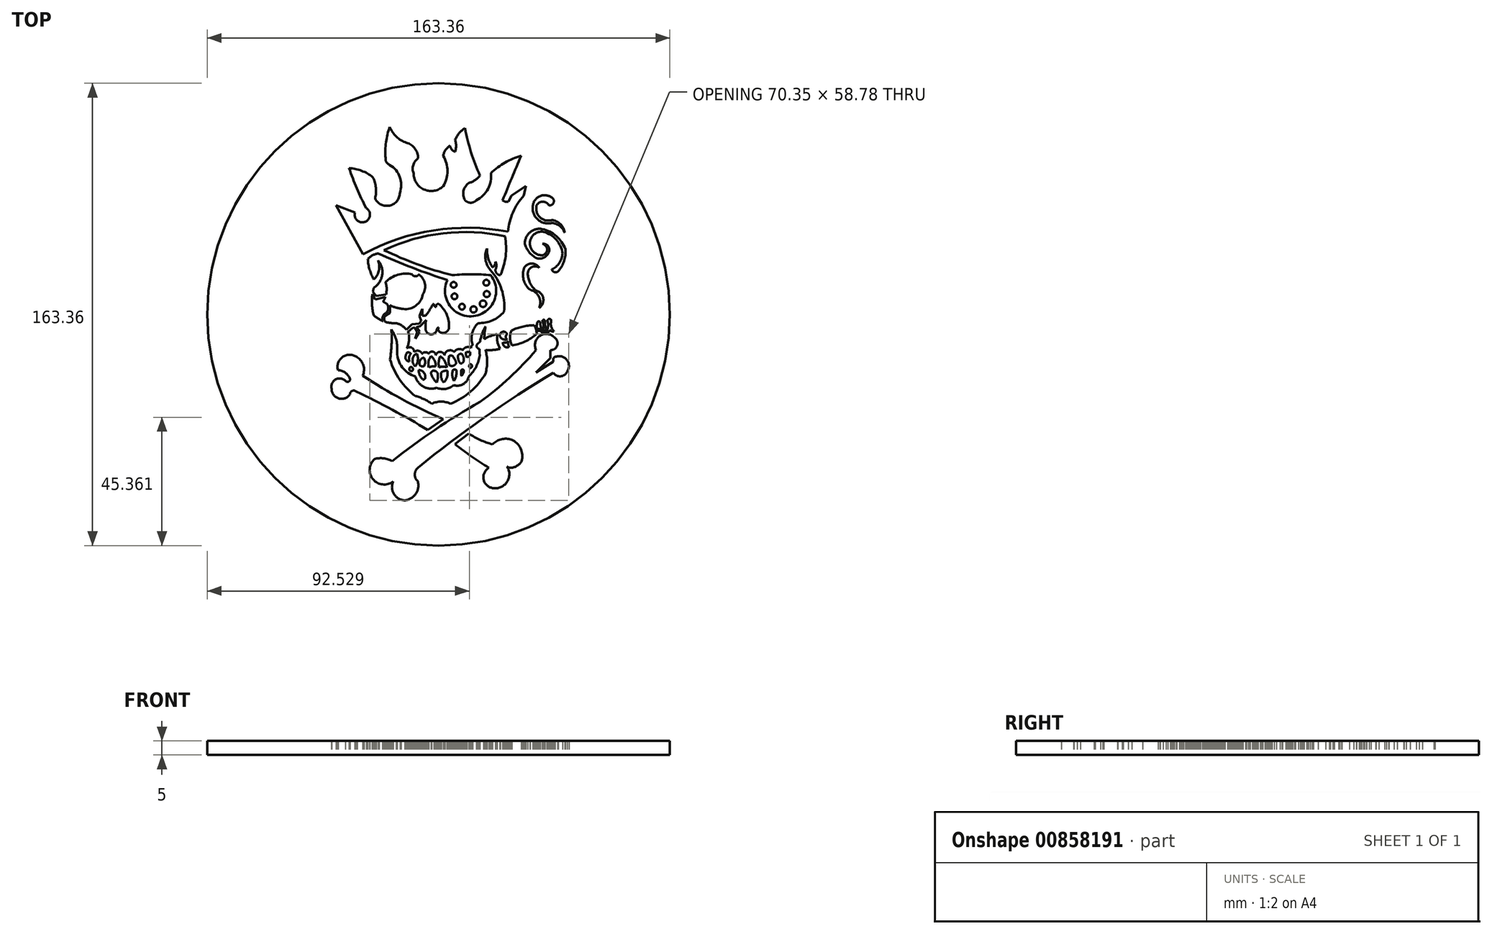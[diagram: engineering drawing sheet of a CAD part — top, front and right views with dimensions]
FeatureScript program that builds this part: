
annotation { "Feature Type Name" : "Feature", "Feature Type Description" : "" }
export const myFeature = defineFeature(function(context is Context, id is Id, definition is map)
    precondition{}
    {
        {
            var Q0;
            Q0=qCreatedBy(makeId("Top.planeOp"),FACE);
            var sketch = newSketch(context, id + "F0", { "sketchPlane" : qUnion([Q0])});
            skArc(sketch, "E0", {"start": v(13.8, 25.5) * mm, "mid": v(-12.46, 25.97) * mm, "end": v(-37.31, 17.5) * mm});
            skLineSegment(sketch, "E1", {"start": v(-37.31, 17.5) * mm, "end": v(-46.9, 34.83) * mm});
            skLineSegment(sketch, "E2", {"start": v(-46.9, 34.83) * mm, "end": v(-40.16, 32.25) * mm});
            skArc(sketch, "E3", {"start": v(-40.16, 32.25) * mm, "mid": v(-36.57, 28.99) * mm, "end": v(-36.23, 33.82) * mm});
            skArc(sketch, "E4", {"start": v(-42.3, 47.97) * mm, "mid": v(-39.5, 40.8) * mm, "end": v(-36.23, 33.82) * mm});
            skArc(sketch, "E5", {"start": v(-33.87, 44.72) * mm, "mid": v(-37.82, 47.02) * mm, "end": v(-42.3, 47.97) * mm});
            skArc(sketch, "E6", {"start": v(-33.08, 37.2) * mm, "mid": v(-32.8, 41.02) * mm, "end": v(-33.87, 44.72) * mm});
            skArc(sketch, "E7", {"start": v(-33.08, 37.2) * mm, "mid": v(-27.9, 34.75) * mm, "end": v(-24.32, 39.21) * mm});
            skArc(sketch, "E8", {"start": v(-24.32, 39.21) * mm, "mid": v(-24.35, 44.8) * mm, "end": v(-27.9, 49.1) * mm});
            skPoint(sketch, "E8.endSnap0", {"position": v(-27.9, 34.75) * mm});
            skArc(sketch, "E9", {"start": v(-29.37, 51.56) * mm, "mid": v(-29.09, 50.06) * mm, "end": v(-27.9, 49.1) * mm});
            skArc(sketch, "E10", {"start": v(-27.9, 62.52) * mm, "mid": v(-29.24, 57.12) * mm, "end": v(-29.37, 51.56) * mm});
            skArc(sketch, "E11", {"start": v(-27.9, 62.52) * mm, "mid": v(-25.56, 59.08) * mm, "end": v(-22, 56.93) * mm});
            skArc(sketch, "E12", {"start": v(-17.88, 51.45) * mm, "mid": v(-19, 54.89) * mm, "end": v(-22, 56.93) * mm});
            skArc(sketch, "E13", {"start": v(-17.88, 51.45) * mm, "mid": v(-19.62, 49.04) * mm, "end": v(-19.46, 46.07) * mm});
            skArc(sketch, "E14", {"start": v(-19.46, 46.07) * mm, "mid": v(-15.74, 40.37) * mm, "end": v(-9.03, 41.54) * mm});
            skArc(sketch, "E15", {"start": v(-9.03, 41.54) * mm, "mid": v(-7.5, 46.92) * mm, "end": v(-9.03, 52.3) * mm});
            skArc(sketch, "E16", {"start": v(-6.6, 55.88) * mm, "mid": v(-8.21, 54.36) * mm, "end": v(-9.03, 52.3) * mm});
            skArc(sketch, "E17", {"start": v(-6.6, 55.88) * mm, "mid": v(-6.01, 54.55) * mm, "end": v(-4.8, 53.72) * mm});
            skArc(sketch, "E18", {"start": v(-4.8, 53.72) * mm, "mid": v(-4.48, 55.86) * mm, "end": v(-4.8, 57.99) * mm});
            skArc(sketch, "E19", {"start": v(-1.33, 62.1) * mm, "mid": v(-3.4, 60.32) * mm, "end": v(-4.8, 57.99) * mm});
            skArc(sketch, "E20", {"start": v(-1.33, 62.1) * mm, "mid": v(0.8, 53.56) * mm, "end": v(3.94, 45.34) * mm});
            skArc(sketch, "E21", {"start": v(0, 42.7) * mm, "mid": v(2.2, 43.68) * mm, "end": v(3.94, 45.34) * mm});
            skArc(sketch, "E22", {"start": v(0, 42.7) * mm, "mid": v(-1.87, 39.9) * mm, "end": v(-1.33, 36.59) * mm});
            skArc(sketch, "E23", {"start": v(-1.33, 36.59) * mm, "mid": v(0.67, 35.74) * mm, "end": v(2.67, 36.59) * mm});
            skArc(sketch, "E24", {"start": v(2.67, 36.59) * mm, "mid": v(6.78, 40.63) * mm, "end": v(7.84, 46.29) * mm});
            skArc(sketch, "E25", {"start": v(18.48, 52.3) * mm, "mid": v(12.8, 49.92) * mm, "end": v(7.84, 46.29) * mm});
            skArc(sketch, "E26", {"start": v(18.48, 52.3) * mm, "mid": v(15.18, 44.46) * mm, "end": v(11.95, 36.59) * mm});
            skArc(sketch, "E27", {"start": v(11.95, 36.59) * mm, "mid": v(12.92, 36.1) * mm, "end": v(14, 36.13) * mm});
            skLineSegment(sketch, "E28", {"start": v(14, 36.13) * mm, "end": v(15.12, 38.22) * mm});
            skLineSegment(sketch, "E29", {"start": v(15.12, 38.22) * mm, "end": v(20.17, 41.67) * mm});
            skLineSegment(sketch, "E30", {"start": v(20.17, 41.67) * mm, "end": v(19.45, 38.22) * mm});
            skArc(sketch, "E31", {"start": v(19.45, 38.22) * mm, "mid": v(15.6, 32.32) * mm, "end": v(13.8, 25.5) * mm});
            skLineSegment(sketch, "E32", {"start": v(-36.21, 27.7) * mm, "end": v(-36.21, 24.14) * mm});
            skLineSegment(sketch, "E33", {"start": v(-36.21, 24.14) * mm, "end": v(-33.76, 22.8) * mm});
            skLineSegment(sketch, "E34", {"start": v(-33.76, 22.8) * mm, "end": v(-33.76, 26.36) * mm});
            skLineSegment(sketch, "E35", {"start": v(-33.76, 26.36) * mm, "end": v(-36.21, 27.7) * mm});
            skLineSegment(sketch, "E36", {"start": v(-26.55, 33.4) * mm, "end": v(-26.55, 29.53) * mm});
            skLineSegment(sketch, "E37", {"start": v(-26.55, 29.53) * mm, "end": v(-24.1, 27.7) * mm});
            skLineSegment(sketch, "E38", {"start": v(-24.1, 27.7) * mm, "end": v(-23.14, 31.27) * mm});
            skLineSegment(sketch, "E39", {"start": v(-23.14, 31.27) * mm, "end": v(-26.55, 33.4) * mm});
            skLineSegment(sketch, "E40", {"start": v(-13.16, 38.56) * mm, "end": v(-15.14, 33.4) * mm});
            skLineSegment(sketch, "E41", {"start": v(-15.14, 33.4) * mm, "end": v(-12.37, 30.32) * mm});
            skLineSegment(sketch, "E42", {"start": v(-12.37, 30.32) * mm, "end": v(-9.75, 34.68) * mm});
            skLineSegment(sketch, "E43", {"start": v(-9.75, 34.68) * mm, "end": v(-13.16, 38.56) * mm});
            skLineSegment(sketch, "E44", {"start": v(0, 34.68) * mm, "end": v(-1.75, 32.46) * mm});
            skLineSegment(sketch, "E45", {"start": v(-1.75, 32.46) * mm, "end": v(-0.13, 29.53) * mm});
            skLineSegment(sketch, "E46", {"start": v(-0.13, 29.53) * mm, "end": v(1.42, 32.3) * mm});
            skLineSegment(sketch, "E47", {"start": v(1.42, 32.3) * mm, "end": v(0, 34.68) * mm});
            skLineSegment(sketch, "E48", {"start": v(11.4, 34.68) * mm, "end": v(9.26, 32.38) * mm});
            skLineSegment(sketch, "E49", {"start": v(9.26, 32.38) * mm, "end": v(9.98, 28.9) * mm});
            skLineSegment(sketch, "E50", {"start": v(9.98, 28.9) * mm, "end": v(12.75, 31.27) * mm});
            skLineSegment(sketch, "E51", {"start": v(12.75, 31.27) * mm, "end": v(11.4, 34.68) * mm});
            skArc(sketch, "E52", {"start": v(12.76, 23.86) * mm, "mid": v(-8.99, 24.94) * mm, "end": v(-29.94, 19) * mm});
            skArc(sketch, "E53", {"start": v(-29.94, 19) * mm, "mid": v(-18.11, 13.95) * mm, "end": v(-5.84, 10.12) * mm});
            skArc(sketch, "E54", {"start": v(7.8, 10.12) * mm, "mid": v(0.98, 10.45) * mm, "end": v(-5.84, 10.12) * mm});
            skArc(sketch, "E55", {"start": v(-7.53, 8.43) * mm, "mid": v(1.64, -4.36) * mm, "end": v(7.8, 10.12) * mm});
            skArc(sketch, "E56", {"start": v(-32.06, 17.83) * mm, "mid": v(-19.93, 12.77) * mm, "end": v(-7.53, 8.43) * mm});
            skArc(sketch, "E57", {"start": v(11.18, 10.12) * mm, "mid": v(13, 16.87) * mm, "end": v(12.76, 23.86) * mm});
            skArc(sketch, "E58", {"start": v(9.43, 12.24) * mm, "mid": v(9.83, 10.79) * mm, "end": v(11.18, 10.12) * mm});
            skArc(sketch, "E59", {"start": v(9.43, 12.24) * mm, "mid": v(9.78, 13.55) * mm, "end": v(9.43, 14.85) * mm});
            skArc(sketch, "E60", {"start": v(8.34, 12.9) * mm, "mid": v(9.14, 13.74) * mm, "end": v(9.43, 14.85) * mm});
            skArc(sketch, "E61", {"start": v(6.4, 19.57) * mm, "mid": v(6.87, 16.1) * mm, "end": v(8.34, 12.9) * mm});
            skArc(sketch, "E62", {"start": v(6.4, 19.57) * mm, "mid": v(5.92, 15.6) * mm, "end": v(7.63, 11.97) * mm});
            skArc(sketch, "E63", {"start": v(12.45, -2.77) * mm, "mid": v(11.59, 5.1) * mm, "end": v(7.63, 11.97) * mm});
            skArc(sketch, "E64", {"start": v(3.3, -6.8) * mm, "mid": v(8.34, -5.85) * mm, "end": v(12.45, -2.77) * mm});
            skArc(sketch, "E65", {"start": v(3.3, -6.8) * mm, "mid": v(1.19, -10.42) * mm, "end": v(1.4, -14.61) * mm});
            skArc(sketch, "E66", {"start": v(-32.06, 17.83) * mm, "mid": v(-34.03, 17.11) * mm, "end": v(-35.68, 15.82) * mm});
            skArc(sketch, "E67", {"start": v(-35.68, 15.82) * mm, "mid": v(-35.01, 12.1) * mm, "end": v(-33.52, 8.63) * mm});
            skArc(sketch, "E68", {"start": v(-33.52, 8.63) * mm, "mid": v(-31.78, 11.75) * mm, "end": v(-32.06, 15.32) * mm});
            skArc(sketch, "E69", {"start": v(-33.52, 5.7) * mm, "mid": v(-30.58, 10.17) * mm, "end": v(-32.06, 15.32) * mm});
            skArc(sketch, "E70", {"start": v(-33.52, 5.7) * mm, "mid": v(-33.73, 4.92) * mm, "end": v(-33.9, 4.15) * mm});
            skArc(sketch, "E71", {"start": v(-33.52, -4.1) * mm, "mid": v(-31.97, -5.26) * mm, "end": v(-30.23, -6.12) * mm});
            skArc(sketch, "E72", {"start": v(-21.14, -10.53) * mm, "mid": v(-21.3, -10.23) * mm, "end": v(-21.46, -9.94) * mm});
            skArc(sketch, "E73", {"start": v(-21.87, -15.65) * mm, "mid": v(-21.14, -13.14) * mm, "end": v(-21.14, -10.53) * mm});
            skArc(sketch, "E74", {"start": v(-19.28, -17) * mm, "mid": v(-20.15, -15.5) * mm, "end": v(-21.87, -15.65) * mm});
            skArc(sketch, "E75", {"start": v(-16.48, -17.67) * mm, "mid": v(-17.7, -16.6) * mm, "end": v(-19.28, -17) * mm});
            skArc(sketch, "E76", {"start": v(-14.2, -17.67) * mm, "mid": v(-15.34, -17.07) * mm, "end": v(-16.48, -17.67) * mm});
            skArc(sketch, "E77", {"start": v(-11.66, -18.14) * mm, "mid": v(-12.74, -16.89) * mm, "end": v(-14.2, -17.67) * mm});
            skArc(sketch, "E78", {"start": v(-8.6, -18.14) * mm, "mid": v(-10.13, -16.95) * mm, "end": v(-11.66, -18.14) * mm});
            skArc(sketch, "E79", {"start": v(-5.12, -17) * mm, "mid": v(-7.2, -16.5) * mm, "end": v(-8.6, -18.14) * mm});
            skArc(sketch, "E80", {"start": v(-2.12, -16.33) * mm, "mid": v(-3.77, -16) * mm, "end": v(-5.12, -17) * mm});
            skArc(sketch, "E81", {"start": v(0.84, -15.55) * mm, "mid": v(-0.8, -15.3) * mm, "end": v(-2.12, -16.33) * mm});
            skArc(sketch, "E82", {"start": v(1.4, -14.61) * mm, "mid": v(0.9, -14.95) * mm, "end": v(0.84, -15.55) * mm});
            skArc(sketch, "E83", {"start": v(-27.81, -19.66) * mm, "mid": v(-27.26, -14.38) * mm, "end": v(-27.3, -9.06) * mm});
            skArc(sketch, "E84", {"start": v(-27.81, -19.66) * mm, "mid": v(-24.35, -26.81) * mm, "end": v(-18.87, -32.57) * mm});
            skArc(sketch, "E85", {"start": v(-13.1, -35.3) * mm, "mid": v(-15.86, -33.66) * mm, "end": v(-18.87, -32.57) * mm});
            skArc(sketch, "E86", {"start": v(-6.4, -35.3) * mm, "mid": v(-9.75, -34.54) * mm, "end": v(-13.1, -35.3) * mm});
            skArc(sketch, "E87", {"start": v(-6.4, -35.3) * mm, "mid": v(0.68, -30.98) * mm, "end": v(5.93, -24.57) * mm});
            skArc(sketch, "E88", {"start": v(5.93, -24.57) * mm, "mid": v(6.49, -20.45) * mm, "end": v(5.93, -16.33) * mm});
            skArc(sketch, "E89", {"start": v(5.93, -8.04) * mm, "mid": v(5.5, -12.18) * mm, "end": v(5.93, -16.33) * mm});
            skArc(sketch, "E90", {"start": v(5.93, -8.04) * mm, "mid": v(4.07, -12.92) * mm, "end": v(3.9, -18.14) * mm});
            skArc(sketch, "E91", {"start": v(0, -25.6) * mm, "mid": v(2.6, -22.22) * mm, "end": v(3.9, -18.14) * mm});
            skArc(sketch, "E92", {"start": v(-5.34, -28.72) * mm, "mid": v(-1.97, -28.37) * mm, "end": v(0, -25.6) * mm});
            skArc(sketch, "E93", {"start": v(-11.26, -29.62) * mm, "mid": v(-8.16, -30.06) * mm, "end": v(-5.34, -28.72) * mm});
            skArc(sketch, "E94", {"start": v(-18.87, -25.6) * mm, "mid": v(-15.95, -29.29) * mm, "end": v(-11.26, -29.62) * mm});
            skArc(sketch, "E95", {"start": v(-25.32, -17.17) * mm, "mid": v(-23.49, -22.45) * mm, "end": v(-18.87, -25.6) * mm});
            skArc(sketch, "E96", {"start": v(-25.32, -17.17) * mm, "mid": v(-25.59, -12.94) * mm, "end": v(-27.3, -9.06) * mm});
            skArc(sketch, "E97", {"start": v(-12.39, 0) * mm, "mid": v(-13.39, -1.39) * mm, "end": v(-14.19, -2.9) * mm});
            skArc(sketch, "E98", {"start": v(-15.25, -9.06) * mm, "mid": v(-13.26, -10.77) * mm, "end": v(-11.26, -9.06) * mm});
            skArc(sketch, "E99", {"start": v(-10.65, -8.35) * mm, "mid": v(-11.08, -8.6) * mm, "end": v(-11.26, -9.06) * mm});
            skArc(sketch, "E100", {"start": v(-10.65, -8.35) * mm, "mid": v(-10.64, -9.5) * mm, "end": v(-9.72, -10.18) * mm});
            skArc(sketch, "E101", {"start": v(-9.72, -10.18) * mm, "mid": v(-7.9, -9.92) * mm, "end": v(-6.95, -8.35) * mm});
            skArc(sketch, "E102", {"start": v(-6.95, -8.35) * mm, "mid": v(-7.8, -3.74) * mm, "end": v(-10.65, 0) * mm});
            skArc(sketch, "E103", {"start": v(-10.65, 0) * mm, "mid": v(-11.39, -0.35) * mm, "end": v(-11.56, -1.15) * mm});
            skArc(sketch, "E104", {"start": v(-12.39, 0) * mm, "mid": v(-12.18, -0.73) * mm, "end": v(-11.56, -1.15) * mm});
            skArc(sketch, "E105", {"start": v(-39.42, -18.9) * mm, "mid": v(-44.45, -18.7) * mm, "end": v(-46.17, -23.44) * mm});
            skArc(sketch, "E106", {"start": v(-37.46, -25.34) * mm, "mid": v(-37.22, -21.75) * mm, "end": v(-39.42, -18.9) * mm});
            skArc(sketch, "E107", {"start": v(-41.96, -26.61) * mm, "mid": v(-43.56, -24.36) * mm, "end": v(-46.17, -23.44) * mm});
            skArc(sketch, "E108", {"start": v(-43.53, -27.2) * mm, "mid": v(-42.51, -27.52) * mm, "end": v(-41.96, -26.61) * mm});
            skArc(sketch, "E109", {"start": v(-43.53, -27.2) * mm, "mid": v(-47.03, -26.72) * mm, "end": v(-48.46, -29.95) * mm});
            skArc(sketch, "E110", {"start": v(-48.46, -29.95) * mm, "mid": v(-45.97, -33.42) * mm, "end": v(-41.96, -31.94) * mm});
            skArc(sketch, "E111", {"start": v(-39.8, -30.95) * mm, "mid": v(-41.19, -30.77) * mm, "end": v(-41.96, -31.94) * mm});
            skArc(sketch, "E112", {"start": v(-37.46, -25.34) * mm, "mid": v(-23.6, -33.65) * mm, "end": v(-9.07, -40.73) * mm});
            skArc(sketch, "E113", {"start": v(-14.44, -44.58) * mm, "mid": v(-26.95, -37.45) * mm, "end": v(-39.8, -30.95) * mm});
            skLineSegment(sketch, "E114", {"start": v(-14.44, -44.58) * mm, "end": v(-9.07, -40.73) * mm});
            skLineSegment(sketch, "E115", {"start": v(-4.87, -49.57) * mm, "end": v(0, -45.87) * mm});
            skArc(sketch, "E116", {"start": v(0, -45.87) * mm, "mid": v(4.04, -48.1) * mm, "end": v(8.4, -49.62) * mm});
            skArc(sketch, "E117", {"start": v(15.06, -47.95) * mm, "mid": v(11.5, -47.85) * mm, "end": v(8.4, -49.62) * mm});
            skArc(sketch, "E118", {"start": v(18.64, -55.58) * mm, "mid": v(18.27, -51.1) * mm, "end": v(15.06, -47.95) * mm});
            skArc(sketch, "E119", {"start": v(14.55, -57.9) * mm, "mid": v(16.92, -57.32) * mm, "end": v(18.64, -55.58) * mm});
            skArc(sketch, "E120", {"start": v(12.96, -56.54) * mm, "mid": v(13.53, -57.49) * mm, "end": v(14.55, -57.9) * mm});
            skArc(sketch, "E121", {"start": v(8.4, -65.08) * mm, "mid": v(13.47, -62.98) * mm, "end": v(13.53, -57.49) * mm});
            skArc(sketch, "E122", {"start": v(7.1, -57.9) * mm, "mid": v(5.22, -61.95) * mm, "end": v(8.4, -65.08) * mm});
            skArc(sketch, "E123", {"start": v(-4.87, -49.57) * mm, "mid": v(0.98, -53.93) * mm, "end": v(7.1, -57.9) * mm});
            skArc(sketch, "E124", {"start": v(3.94, -34.69) * mm, "mid": v(-11.96, -44.52) * mm, "end": v(-27.03, -55.58) * mm});
            skArc(sketch, "E125", {"start": v(3.94, -34.69) * mm, "mid": v(14.4, -26.1) * mm, "end": v(23.76, -16.33) * mm});
            skArc(sketch, "E126", {"start": v(30.4, -12.04) * mm, "mid": v(25.2, -11.26) * mm, "end": v(23.76, -16.33) * mm});
            skArc(sketch, "E127", {"start": v(28.83, -16.33) * mm, "mid": v(31.22, -14.77) * mm, "end": v(30.4, -12.04) * mm});
            skLineSegment(sketch, "E128", {"start": v(28.83, -16.33) * mm, "end": v(28.83, -19.16) * mm});
            skLineSegment(sketch, "E129", {"start": v(28.83, -19.16) * mm, "end": v(23.7, -24.3) * mm});
            skLineSegment(sketch, "E130", {"start": v(23.7, -24.3) * mm, "end": v(29.82, -20.4) * mm});
            skLineSegment(sketch, "E131", {"start": v(29.82, -20.4) * mm, "end": v(29.82, -19.16) * mm});
            skArc(sketch, "E132", {"start": v(34.79, -23.88) * mm, "mid": v(34.3, -19.43) * mm, "end": v(29.82, -19.16) * mm});
            skArc(sketch, "E133", {"start": v(29.82, -24.38) * mm, "mid": v(32.45, -25.6) * mm, "end": v(34.79, -23.88) * mm});
            skArc(sketch, "E134", {"start": v(29.82, -24.38) * mm, "mid": v(5.32, -40.3) * mm, "end": v(-17.98, -57.94) * mm});
            skArc(sketch, "E135", {"start": v(-17.98, -57.94) * mm, "mid": v(-19.07, -60.36) * mm, "end": v(-17.98, -62.78) * mm});
            skArc(sketch, "E136", {"start": v(-22.63, -69.45) * mm, "mid": v(-18.76, -67.19) * mm, "end": v(-17.98, -62.78) * mm});
            skArc(sketch, "E137", {"start": v(-26.7, -62.78) * mm, "mid": v(-26.45, -67.2) * mm, "end": v(-22.63, -69.45) * mm});
            skArc(sketch, "E138", {"start": v(-33.28, -54.82) * mm, "mid": v(-33.83, -61.96) * mm, "end": v(-26.7, -62.78) * mm});
            skArc(sketch, "E139", {"start": v(-27.03, -55.58) * mm, "mid": v(-30.08, -54.58) * mm, "end": v(-33.28, -54.82) * mm});
            skCircle(sketch, "E140", {"center": v(-10.67, -3.74) * mm, "radius": 81.68 * mm});
            skPoint(sketch, "E140.centerSnap0", {"position": v(-7.8, -3.74) * mm});
            skArc(sketch, "E141", {"start": v(-21.74, -17.17) * mm, "mid": v(-22.26, -18.2) * mm, "end": v(-22.31, -19.36) * mm});
            skArc(sketch, "E142", {"start": v(-22.31, -19.36) * mm, "mid": v(-21.8, -20.1) * mm, "end": v(-20.93, -20.33) * mm});
            skArc(sketch, "E143", {"start": v(-20.44, -17.65) * mm, "mid": v(-21.11, -18.91) * mm, "end": v(-20.93, -20.33) * mm});
            skArc(sketch, "E144", {"start": v(-20.44, -17.65) * mm, "mid": v(-21.02, -17.22) * mm, "end": v(-21.74, -17.17) * mm});
            skArc(sketch, "E145", {"start": v(-18.32, -17.65) * mm, "mid": v(-19.16, -18.08) * mm, "end": v(-19.65, -18.89) * mm});
            skArc(sketch, "E146", {"start": v(-19.65, -18.89) * mm, "mid": v(-19.8, -20.63) * mm, "end": v(-18.9, -22.12) * mm});
            skArc(sketch, "E147", {"start": v(-18.9, -22.12) * mm, "mid": v(-18, -19.96) * mm, "end": v(-18.32, -17.65) * mm});
            skArc(sketch, "E148", {"start": v(-15.88, -19) * mm, "mid": v(-17.2, -20) * mm, "end": v(-17.3, -21.64) * mm});
            skArc(sketch, "E149", {"start": v(-15.88, -22.12) * mm, "mid": v(-15.38, -20.57) * mm, "end": v(-15.88, -19) * mm});
            skArc(sketch, "E150", {"start": v(-17.3, -21.64) * mm, "mid": v(-16.66, -22.07) * mm, "end": v(-15.88, -22.12) * mm});
            skArc(sketch, "E151", {"start": v(-13.35, -18.46) * mm, "mid": v(-14.22, -20.36) * mm, "end": v(-14.13, -22.45) * mm});
            skArc(sketch, "E152", {"start": v(-11.64, -22.12) * mm, "mid": v(-12.07, -20.1) * mm, "end": v(-13.35, -18.46) * mm});
            skArc(sketch, "E153", {"start": v(-11.64, -22.12) * mm, "mid": v(-12.9, -22.12) * mm, "end": v(-14.13, -22.45) * mm});
            skArc(sketch, "E154", {"start": v(-10.13, -18.53) * mm, "mid": v(-10.6, -20.46) * mm, "end": v(-10.5, -22.45) * mm});
            skArc(sketch, "E155", {"start": v(-7.73, -22.45) * mm, "mid": v(-8.5, -20.23) * mm, "end": v(-10.13, -18.53) * mm});
            skArc(sketch, "E156", {"start": v(-7.73, -22.45) * mm, "mid": v(-9.12, -22.21) * mm, "end": v(-10.5, -22.45) * mm});
            skArc(sketch, "E157", {"start": v(-6.92, -18.46) * mm, "mid": v(-7.14, -20.05) * mm, "end": v(-6.92, -21.64) * mm});
            skArc(sketch, "E158", {"start": v(-6.92, -21.64) * mm, "mid": v(-5.52, -21.89) * mm, "end": v(-4.48, -20.92) * mm});
            skArc(sketch, "E159", {"start": v(-4.48, -20.92) * mm, "mid": v(-4.93, -19.59) * mm, "end": v(-5.78, -18.46) * mm});
            skArc(sketch, "E160", {"start": v(-5.78, -18.46) * mm, "mid": v(-6.35, -18.22) * mm, "end": v(-6.92, -18.46) * mm});
            skArc(sketch, "E161", {"start": v(-3.77, -18.22) * mm, "mid": v(-3.66, -19.75) * mm, "end": v(-2.9, -21.1) * mm});
            skPoint(sketch, "E161.startSnap0", {"position": v(-3.77, -16) * mm});
            skPoint(sketch, "E161.startSnap1", {"position": v(-6.35, -18.22) * mm});
            skArc(sketch, "E162", {"start": v(-2.9, -21.1) * mm, "mid": v(-2.3, -20.92) * mm, "end": v(-1.85, -20.49) * mm});
            skArc(sketch, "E163", {"start": v(-1.85, -20.49) * mm, "mid": v(-1.84, -18.95) * mm, "end": v(-2.61, -17.63) * mm});
            skArc(sketch, "E164", {"start": v(-2.61, -17.63) * mm, "mid": v(-3.28, -17.75) * mm, "end": v(-3.77, -18.22) * mm});
            skArc(sketch, "E165", {"start": v(-0.86, -16.93) * mm, "mid": v(-1, -17.92) * mm, "end": v(-0.69, -18.87) * mm});
            skArc(sketch, "E166", {"start": v(-0.69, -18.87) * mm, "mid": v(0.33, -18.21) * mm, "end": v(0.46, -17) * mm});
            skArc(sketch, "E167", {"start": v(-0.86, -16.93) * mm, "mid": v(-0.2, -17.04) * mm, "end": v(0.46, -17) * mm});
            skArc(sketch, "E168", {"start": v(0.46, -22.68) * mm, "mid": v(1.18, -22) * mm, "end": v(0.46, -21.31) * mm});
            skArc(sketch, "E169", {"start": v(0.46, -21.31) * mm, "mid": v(0.15, -22) * mm, "end": v(0.46, -22.68) * mm});
            skArc(sketch, "E170", {"start": v(-2.61, -23.42) * mm, "mid": v(-2.75, -24.42) * mm, "end": v(-2.61, -25.42) * mm});
            skArc(sketch, "E171", {"start": v(-2.61, -25.42) * mm, "mid": v(-1.93, -24.51) * mm, "end": v(-1.8, -23.39) * mm});
            skArc(sketch, "E172", {"start": v(-1.8, -23.39) * mm, "mid": v(-2.21, -23.19) * mm, "end": v(-2.61, -23.42) * mm});
            skArc(sketch, "E173", {"start": v(-5.62, -23.42) * mm, "mid": v(-5.8, -25.36) * mm, "end": v(-5.23, -27.21) * mm});
            skArc(sketch, "E174", {"start": v(-4.37, -23.42) * mm, "mid": v(-5, -23.19) * mm, "end": v(-5.62, -23.42) * mm});
            skArc(sketch, "E175", {"start": v(-5.23, -27.21) * mm, "mid": v(-4.45, -25.4) * mm, "end": v(-4.37, -23.42) * mm});
            skArc(sketch, "E176", {"start": v(-9.71, -24.2) * mm, "mid": v(-9.74, -26.1) * mm, "end": v(-8.83, -27.76) * mm});
            skArc(sketch, "E177", {"start": v(-7.54, -23.7) * mm, "mid": v(-8.68, -23.72) * mm, "end": v(-9.71, -24.2) * mm});
            skArc(sketch, "E178", {"start": v(-8.83, -27.76) * mm, "mid": v(-7.66, -25.9) * mm, "end": v(-7.54, -23.7) * mm});
            skArc(sketch, "E179", {"start": v(-10.94, -25.2) * mm, "mid": v(-11.18, -24.2) * mm, "end": v(-12.07, -23.7) * mm});
            skArc(sketch, "E180", {"start": v(-11.29, -27.76) * mm, "mid": v(-10.98, -26.5) * mm, "end": v(-10.94, -25.2) * mm});
            skArc(sketch, "E181", {"start": v(-12.07, -23.7) * mm, "mid": v(-13.04, -23.86) * mm, "end": v(-13.24, -24.82) * mm});
            skArc(sketch, "E182", {"start": v(-13.24, -24.82) * mm, "mid": v(-12.5, -26.45) * mm, "end": v(-11.29, -27.76) * mm});
            skArc(sketch, "E183", {"start": v(-17.66, -23.39) * mm, "mid": v(-17.3, -25.2) * mm, "end": v(-16.25, -26.74) * mm});
            skArc(sketch, "E184", {"start": v(-15.43, -26.35) * mm, "mid": v(-15.84, -24.34) * mm, "end": v(-17.66, -23.39) * mm});
            skArc(sketch, "E185", {"start": v(-16.25, -26.74) * mm, "mid": v(-15.78, -26.68) * mm, "end": v(-15.43, -26.35) * mm});
            skArc(sketch, "E186", {"start": v(-20.31, -22.3) * mm, "mid": v(-21.01, -23.18) * mm, "end": v(-20, -23.7) * mm});
            skArc(sketch, "E187", {"start": v(-20, -23.7) * mm, "mid": v(-19.74, -22.9) * mm, "end": v(-20.31, -22.3) * mm});
            skArc(sketch, "E188", {"start": v(-30.23, 0.8) * mm, "mid": v(-29.8, 1.61) * mm, "end": v(-29.45, 2.47) * mm});
            skPoint(sketch, "E188.startSnap0", {"position": v(-34.22, 0.8) * mm});
            skArc(sketch, "E189", {"start": v(-20, 10.42) * mm, "mid": v(-25.04, 10.28) * mm, "end": v(-29.38, 7.7) * mm});
            skArc(sketch, "E190", {"start": v(-20, 10.42) * mm, "mid": v(-18.83, 9.73) * mm, "end": v(-17.66, 10.42) * mm});
            skArc(sketch, "E191", {"start": v(-16.25, 3.28) * mm, "mid": v(-15.5, 7.14) * mm, "end": v(-17.66, 10.42) * mm});
            skArc(sketch, "E192", {"start": v(-23.17, -1.82) * mm, "mid": v(-18.7, -0.65) * mm, "end": v(-16.25, 3.28) * mm});
            skArc(sketch, "E193", {"start": v(-30.23, 0.8) * mm, "mid": v(-29.58, 0.38) * mm, "end": v(-28.92, 0) * mm});
            skArc(sketch, "E194", {"start": v(-29.52, -3.4) * mm, "mid": v(-30.41, -4.62) * mm, "end": v(-30.23, -6.12) * mm});
            skArc(sketch, "E195", {"start": v(-29.52, -3.4) * mm, "mid": v(-28.47, -1.84) * mm, "end": v(-28.92, 0) * mm});
            skArc(sketch, "E196", {"start": v(-29.52, -4.23) * mm, "mid": v(-29.85, -5.3) * mm, "end": v(-29.52, -6.36) * mm});
            skLineSegment(sketch, "E197", {"start": v(-29.52, -4.23) * mm, "end": v(-27.88, -3.11) * mm});
            skLineSegment(sketch, "E198", {"start": v(-27.88, -3.11) * mm, "end": v(-27.88, -0.52) * mm});
            skArc(sketch, "E199.trimOffspring", {"start": v(-29.52, -6.36) * mm, "mid": v(-27.64, -6.75) * mm, "end": v(-25.71, -6.8) * mm});
            skArc(sketch, "E200.trimOffspring", {"start": v(-27.88, -0.52) * mm, "mid": v(-25.57, -1.35) * mm, "end": v(-23.17, -1.82) * mm});
            skLineSegment(sketch, "E201", {"start": v(-33.9, 4.15) * mm, "end": v(-32.65, 2.85) * mm});
            skLineSegment(sketch, "E202", {"start": v(-32.65, 2.85) * mm, "end": v(-29.2, 3.37) * mm});
            skLineSegment(sketch, "E203", {"start": v(-34, 3.5) * mm, "end": v(-33.06, 1.51) * mm});
            skPoint(sketch, "E203.startSnap0", {"position": v(-33.27, 3.5) * mm});
            skLineSegment(sketch, "E204", {"start": v(-33.06, 1.51) * mm, "end": v(-29.45, 2.47) * mm});
            skArc(sketch, "E205.trimOffspring", {"start": v(-29.2, 3.37) * mm, "mid": v(-29.01, 5.55) * mm, "end": v(-29.38, 7.7) * mm});
            skArc(sketch, "E206.trimOffspring", {"start": v(-34, 3.5) * mm, "mid": v(-34.18, -0.33) * mm, "end": v(-33.52, -4.1) * mm});
            skArc(sketch, "E207", {"start": v(10.07, -10.7) * mm, "mid": v(6.37, -11.95) * mm, "end": v(3.12, -14.12) * mm});
            skArc(sketch, "E208", {"start": v(3.12, -14.12) * mm, "mid": v(2.8, -15.09) * mm, "end": v(3.45, -15.87) * mm});
            skArc(sketch, "E209", {"start": v(3.45, -15.87) * mm, "mid": v(7.26, -16.36) * mm, "end": v(11.08, -15.87) * mm});
            skArc(sketch, "E210", {"start": v(10.07, -10.7) * mm, "mid": v(10.1, -13.38) * mm, "end": v(11.08, -15.87) * mm});
            skArc(sketch, "E211", {"start": v(13.53, -10.7) * mm, "mid": v(11.78, -9.93) * mm, "end": v(11.08, -11.7) * mm});
            skArc(sketch, "E212", {"start": v(13.53, -10.7) * mm, "mid": v(13.08, -11.64) * mm, "end": v(13.53, -12.58) * mm});
            skArc(sketch, "E213", {"start": v(11.08, -11.7) * mm, "mid": v(12.17, -12.52) * mm, "end": v(13.53, -12.58) * mm});
            skArc(sketch, "E214", {"start": v(12.08, -13.62) * mm, "mid": v(13.08, -13.69) * mm, "end": v(13.93, -13.18) * mm});
            skArc(sketch, "E215", {"start": v(13.93, -13.18) * mm, "mid": v(13.9, -14.2) * mm, "end": v(14.27, -15.17) * mm});
            skArc(sketch, "E216", {"start": v(12.08, -13.62) * mm, "mid": v(12.67, -15.1) * mm, "end": v(14.27, -15.17) * mm});
            skArc(sketch, "E217", {"start": v(15.04, -9.42) * mm, "mid": v(14.6, -12.06) * mm, "end": v(15.18, -14.66) * mm});
            skArc(sketch, "E218", {"start": v(15.18, -14.66) * mm, "mid": v(19.84, -13.33) * mm, "end": v(23.9, -10.7) * mm});
            skArc(sketch, "E219", {"start": v(23.04, -7.54) * mm, "mid": v(18.94, -8.06) * mm, "end": v(15.04, -9.42) * mm});
            skArc(sketch, "E220", {"start": v(23.9, -10.7) * mm, "mid": v(23.77, -9.04) * mm, "end": v(23.04, -7.54) * mm});
            skArc(sketch, "E221", {"start": v(24.24, -6.64) * mm, "mid": v(24.02, -8.31) * mm, "end": v(24.68, -9.87) * mm});
            skArc(sketch, "E222", {"start": v(25.24, -6.64) * mm, "mid": v(24.74, -6.15) * mm, "end": v(24.24, -6.64) * mm});
            skArc(sketch, "E223", {"start": v(25.24, -6.64) * mm, "mid": v(25.48, -8.23) * mm, "end": v(26.05, -9.73) * mm});
            skArc(sketch, "E224", {"start": v(26.05, -9.73) * mm, "mid": v(26.41, -7.9) * mm, "end": v(26.05, -6.08) * mm});
            skArc(sketch, "E225", {"start": v(26.86, -6.08) * mm, "mid": v(26.45, -5.62) * mm, "end": v(26.05, -6.08) * mm});
            skArc(sketch, "E226", {"start": v(26.86, -6.08) * mm, "mid": v(27.02, -7.94) * mm, "end": v(27.54, -9.73) * mm});
            skArc(sketch, "E227", {"start": v(27.54, -9.73) * mm, "mid": v(28, -7.93) * mm, "end": v(27.81, -6.08) * mm});
            skArc(sketch, "E228", {"start": v(29.1, -6.08) * mm, "mid": v(28.46, -5.33) * mm, "end": v(27.81, -6.08) * mm});
            skArc(sketch, "E229", {"start": v(29.1, -6.08) * mm, "mid": v(29.12, -8.03) * mm, "end": v(30.1, -9.73) * mm});
            skArc(sketch, "E230", {"start": v(24.87, -8.5) * mm, "mid": v(24.71, -9.18) * mm, "end": v(24.68, -9.87) * mm});
            skArc(sketch, "E231", {"start": v(24.87, -8.5) * mm, "mid": v(25.34, -9.55) * mm, "end": v(26.17, -10.33) * mm});
            skArc(sketch, "E232", {"start": v(26.17, -10.33) * mm, "mid": v(26.57, -9.7) * mm, "end": v(26.8, -8.98) * mm});
            skArc(sketch, "E233", {"start": v(26.8, -8.98) * mm, "mid": v(27, -9.8) * mm, "end": v(27.65, -10.33) * mm});
            skArc(sketch, "E234", {"start": v(27.65, -10.33) * mm, "mid": v(28.25, -9.88) * mm, "end": v(28.7, -9.27) * mm});
            skArc(sketch, "E235", {"start": v(28.7, -9.27) * mm, "mid": v(29.32, -9.73) * mm, "end": v(30.1, -9.73) * mm});
            skArc(sketch, "E236", {"start": v(24.87, -1.4) * mm, "mid": v(24.77, 2.56) * mm, "end": v(21.64, 4.98) * mm});
            skArc(sketch, "E237", {"start": v(19.56, 12.77) * mm, "mid": v(19.35, 8.54) * mm, "end": v(21.64, 4.98) * mm});
            skArc(sketch, "E238", {"start": v(24.87, 12.77) * mm, "mid": v(22.21, 14.27) * mm, "end": v(19.56, 12.77) * mm});
            skArc(sketch, "E239", {"start": v(24.87, 12.77) * mm, "mid": v(22.13, 12.92) * mm, "end": v(20.87, 10.48) * mm});
            skArc(sketch, "E240", {"start": v(20.86, 10.79) * mm, "mid": v(21.64, 7.43) * mm, "end": v(23.71, 4.69) * mm});
            skArc(sketch, "E241", {"start": v(24.87, -1.4) * mm, "mid": v(26.29, 2.03) * mm, "end": v(23.71, 4.69) * mm});
            skPoint(sketch, "E242.orphan", {"position": v(22.21, 8.5) * mm});
            skArc(sketch, "E243", {"start": v(25.94, 17.17) * mm, "mid": v(27.66, 19.18) * mm, "end": v(25.98, 21.22) * mm});
            skArc(sketch, "E244", {"start": v(21.9, 22.95) * mm, "mid": v(22.35, 18.96) * mm, "end": v(25.94, 17.17) * mm});
            skArc(sketch, "E245", {"start": v(28.98, 23.92) * mm, "mid": v(25.16, 25.48) * mm, "end": v(21.9, 22.95) * mm});
            skArc(sketch, "E246", {"start": v(33.09, 17.8) * mm, "mid": v(30.91, 22.65) * mm, "end": v(26.4, 25.46) * mm});
            skArc(sketch, "E247", {"start": v(29.34, 12.18) * mm, "mid": v(32, 14.46) * mm, "end": v(33.09, 17.8) * mm});
            skArc(sketch, "E248", {"start": v(29.34, 12.18) * mm, "mid": v(30.31, 11.2) * mm, "end": v(31.65, 11.56) * mm});
            skArc(sketch, "E249", {"start": v(31.65, 11.56) * mm, "mid": v(33.66, 15.18) * mm, "end": v(34.1, 19.3) * mm});
            skArc(sketch, "E250", {"start": v(34.1, 19.3) * mm, "mid": v(30.94, 23.91) * mm, "end": v(25.94, 26.44) * mm});
            skArc(sketch, "E251", {"start": v(25.94, 26.44) * mm, "mid": v(21.6, 25.28) * mm, "end": v(19.81, 21.15) * mm});
            skArc(sketch, "E252", {"start": v(19.81, 21.15) * mm, "mid": v(21.24, 18.37) * mm, "end": v(23.56, 16.3) * mm});
            skArc(sketch, "E253", {"start": v(23.56, 16.3) * mm, "mid": v(26.4, 16.29) * mm, "end": v(28.33, 18.38) * mm});
            skArc(sketch, "E254", {"start": v(28.33, 18.38) * mm, "mid": v(27.96, 20.47) * mm, "end": v(25.98, 21.22) * mm});
            skArc(sketch, "E255", {"start": v(28.33, 34.8) * mm, "mid": v(26.16, 36.1) * mm, "end": v(23.97, 34.84) * mm});
            skArc(sketch, "E256", {"start": v(23.97, 34.84) * mm, "mid": v(25.06, 30.63) * mm, "end": v(29.29, 29.6) * mm});
            skArc(sketch, "E257", {"start": v(33.83, 25.2) * mm, "mid": v(32.33, 28.2) * mm, "end": v(29.29, 29.6) * mm});
            skArc(sketch, "E258", {"start": v(28.33, 34.8) * mm, "mid": v(29.97, 35.78) * mm, "end": v(29.29, 37.57) * mm});
            skArc(sketch, "E259", {"start": v(29.29, 37.57) * mm, "mid": v(25.43, 38.17) * mm, "end": v(22.75, 35.33) * mm});
            skArc(sketch, "E260", {"start": v(22.75, 35.33) * mm, "mid": v(24.08, 30.08) * mm, "end": v(29.29, 28.59) * mm});
            skArc(sketch, "E261", {"start": v(33.83, 25.2) * mm, "mid": v(32.07, 27.57) * mm, "end": v(29.29, 28.59) * mm});
            skCircle(sketch, "E262", {"center": v(-5.35, 6.7) * mm, "radius": 1 * mm});
            skCircle(sketch, "E263", {"center": v(-5.04, 2.65) * mm, "radius": 1 * mm});
            skCircle(sketch, "E264", {"center": v(-2.39, -1.02) * mm, "radius": 1 * mm});
            skCircle(sketch, "E265", {"center": v(1.68, -1.97) * mm, "radius": 1.1 * mm});
            skCircle(sketch, "E266", {"center": v(5.04, 0.04) * mm, "radius": 1.16 * mm});
            skCircle(sketch, "E267", {"center": v(6.34, 3.45) * mm, "radius": 1.08 * mm});
            skCircle(sketch, "E268", {"center": v(6.2, 7.46) * mm, "radius": 1.02 * mm});
            skLineSegment(sketch, "E269", {"start": v(-21.46, -9.94) * mm, "end": v(-19.85, -8.55) * mm});
            skLineSegment(sketch, "E270", {"start": v(-19.85, -8.55) * mm, "end": v(-19.11, -8.36) * mm});
            skLineSegment(sketch, "E271", {"start": v(-15.06, -5.7) * mm, "end": v(-17.1, -7.85) * mm});
            skLineSegment(sketch, "E272", {"start": v(-22.04, -9.12) * mm, "end": v(-20.08, -7.24) * mm});
            skLineSegment(sketch, "E273", {"start": v(-20.08, -7.24) * mm, "end": v(-17.58, -7) * mm});
            skLineSegment(sketch, "E274", {"start": v(-17.58, -7) * mm, "end": v(-16.82, -6.09) * mm});
            skArc(sketch, "E275.trimOffspring", {"start": v(-15.06, -5.7) * mm, "mid": v(-15.27, -7.37) * mm, "end": v(-15.25, -9.06) * mm});
            skArc(sketch, "E276.trimOffspring", {"start": v(-22.04, -9.12) * mm, "mid": v(-23.7, -7.66) * mm, "end": v(-25.71, -6.8) * mm});
            skLineSegment(sketch, "E277", {"start": v(-19.11, -8.36) * mm, "end": v(-18.16, -9.92) * mm});
            skLineSegment(sketch, "E278", {"start": v(-18.16, -9.92) * mm, "end": v(-18.89, -12.34) * mm});
            skLineSegment(sketch, "E279", {"start": v(-18.89, -12.34) * mm, "end": v(-17.37, -9.85) * mm});
            skLineSegment(sketch, "E280", {"start": v(-17.37, -9.85) * mm, "end": v(-18.47, -8.2) * mm});
            skLineSegment(sketch, "E281", {"start": v(-16.82, -6.09) * mm, "end": v(-17.45, -4.35) * mm});
            skLineSegment(sketch, "E282", {"start": v(-17.45, -4.35) * mm, "end": v(-16.4, -1.77) * mm});
            skLineSegment(sketch, "E283", {"start": v(-16.4, -1.77) * mm, "end": v(-16.4, -4.16) * mm});
            skLineSegment(sketch, "E284", {"start": v(-16.4, -4.16) * mm, "end": v(-15.23, -4.16) * mm});
            skLineSegment(sketch, "E285.trimOffspring", {"start": v(-15.23, -4.16) * mm, "end": v(-14.19, -2.9) * mm});
            skLineSegment(sketch, "E286.trimOffspring", {"start": v(-18.47, -8.2) * mm, "end": v(-17.1, -7.85) * mm});
            skSolve(sketch);
        }
        {
            var Q0;
            Q0=makeQuery(id+"F0.imprint","IMPRINT",FACE,{"disambiguationData":[TD([[makeQuery(id+"F0.imprint","IMPRINT",EDGE,{"derivedFrom":sQuery(id+"F0.wireOp",EDGE,"E0")}),1.0]])]});
            extrude(context, id + "F1", {"entities" : qUnion([Q0]), "depth" : 5 * mm, "offsetDistance" : 25 * mm});
        }
    });
